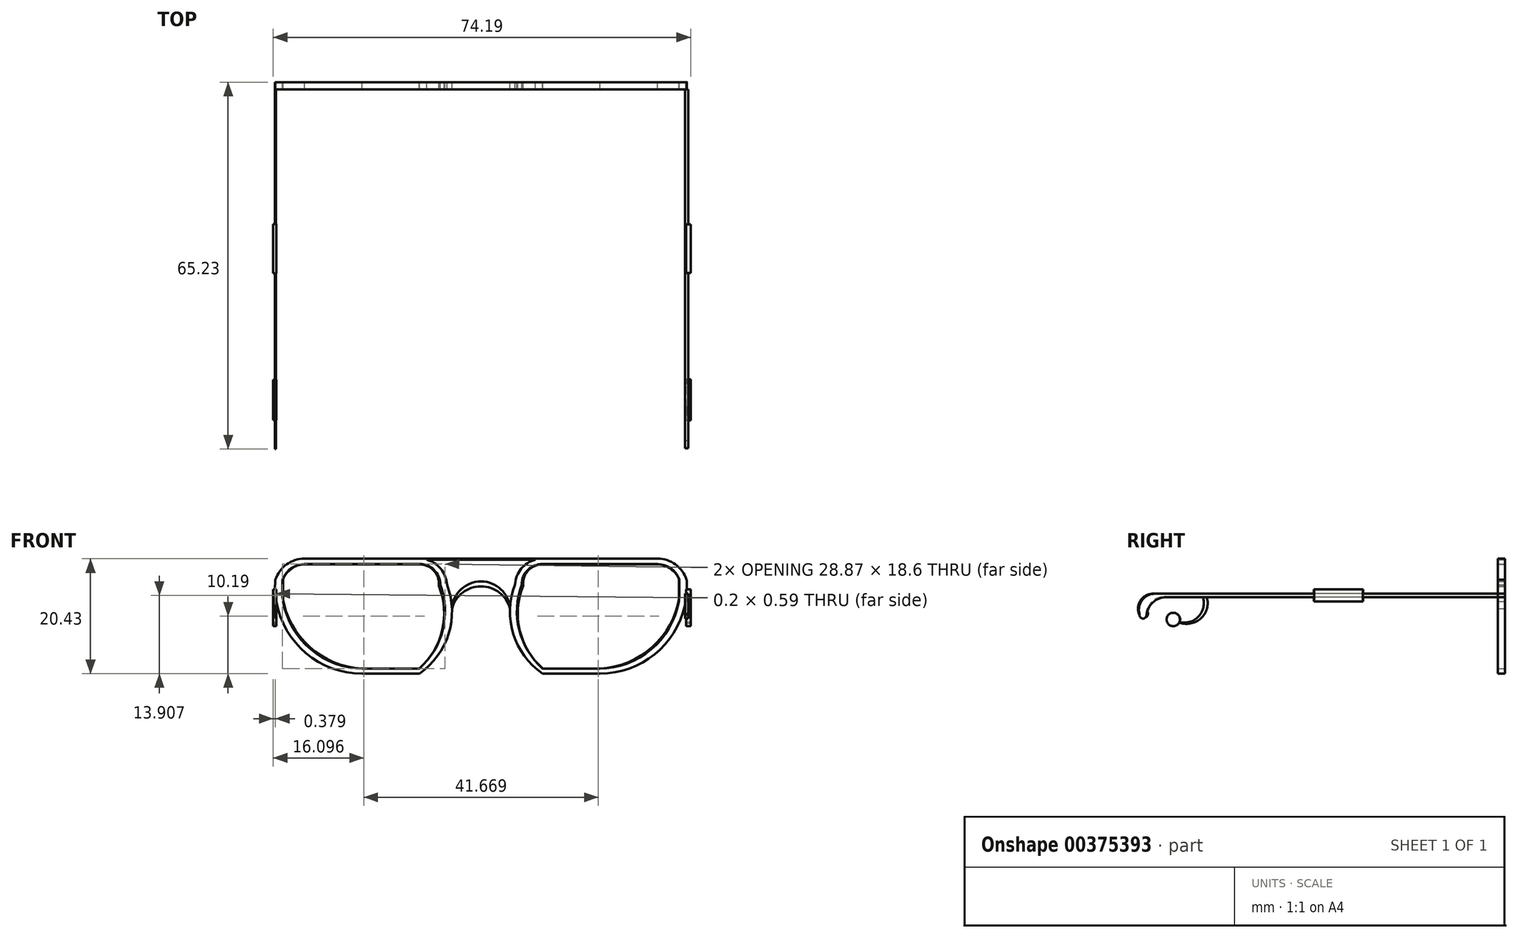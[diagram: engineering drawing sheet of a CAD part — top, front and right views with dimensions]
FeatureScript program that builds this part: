
annotation { "Feature Type Name" : "Feature", "Feature Type Description" : "" }
export const myFeature = defineFeature(function(context is Context, id is Id, definition is map)
    precondition{}
    {
        {
            var Q0;
            Q0=qCreatedBy(makeId("Front.planeOp"),FACE);
            var sketch = newSketch(context, id + "F0", { "sketchPlane" : qUnion([Q0])});
            skLineSegment(sketch, "E0", {"start": v(-10.94, 16.4) * mm, "end": v(-31.37, 16.4) * mm});
            skArc(sketch, "E1", {"start": v(-6.04, 11.8) * mm, "mid": v(-7.58, 15.07) * mm, "end": v(-10.94, 16.4) * mm});
            skArc(sketch, "E2", {"start": v(-10.94, -4.03) * mm, "mid": v(-5.75, 3.04) * mm, "end": v(-6.04, 11.8) * mm});
            skLineSegment(sketch, "E3", {"start": v(-10.94, -4.03) * mm, "end": v(-21.15, -4.03) * mm});
            skPoint(sketch, "E3.endSnap0", {"position": v(-21.15, 16.4) * mm});
            skArc(sketch, "E4", {"start": v(-31.37, 16.4) * mm, "mid": v(-34.57, 15.37) * mm, "end": v(-36.55, 12.66) * mm});
            skArc(sketch, "E5", {"start": v(-36.55, 12.66) * mm, "mid": v(-32.5, 0.94) * mm, "end": v(-21.15, -4.03) * mm});
            skLineSegment(sketch, "E6", {"start": v(0, 26.48) * mm, "end": v(0, -21.87) * mm, "construction": true});
            skArc(sketch, "E7.MirrorCS", {"start": v(6.04, 11.8) * mm, "mid": v(7.58, 15.07) * mm, "end": v(10.94, 16.4) * mm});
            skLineSegment(sketch, "E8.MirrorCS", {"start": v(10.94, 16.4) * mm, "end": v(31.37, 16.4) * mm});
            skArc(sketch, "E9.MirrorCS", {"start": v(31.37, 16.4) * mm, "mid": v(34.57, 15.37) * mm, "end": v(36.55, 12.66) * mm});
            skArc(sketch, "E10.MirrorCS", {"start": v(36.55, 12.66) * mm, "mid": v(32.5, 0.94) * mm, "end": v(21.15, -4.03) * mm});
            skLineSegment(sketch, "E11.MirrorCS", {"start": v(10.94, -4.03) * mm, "end": v(21.15, -4.03) * mm});
            skArc(sketch, "E12.MirrorCS", {"start": v(10.94, -4.03) * mm, "mid": v(5.75, 3.04) * mm, "end": v(6.04, 11.8) * mm});
            skLineSegment(sketch, "E13", {"start": v(-10.94, 16.4) * mm, "end": v(10.94, 16.4) * mm});
            skLineSegment(sketch, "E14", {"start": v(-9.67, 16.24) * mm, "end": v(9.67, 16.24) * mm});
            skPoint(sketch, "E15", {"position": v(-5.16, 7.53) * mm});
            skPoint(sketch, "E16", {"position": v(5.16, 7.53) * mm});
            skArc(sketch, "E17", {"start": v(5.16, 7.53) * mm, "mid": v(0, 12.36) * mm, "end": v(-5.16, 7.53) * mm});
            skArc(sketch, "E18", {"start": v(5.16, 7.53) * mm, "mid": v(0, 11.49) * mm, "end": v(-5.16, 7.53) * mm});
            skLineSegment(sketch, "E19.bottom", {"start": v(36.55, 12.66) * mm, "end": v(35.27, 12.66) * mm});
            skLineSegment(sketch, "E19.top", {"start": v(36.55, 9.58) * mm, "end": v(35.27, 9.58) * mm});
            skLineSegment(sketch, "E19.left", {"start": v(36.55, 12.66) * mm, "end": v(36.55, 9.58) * mm});
            skLineSegment(sketch, "E19.right", {"start": v(35.27, 12.66) * mm, "end": v(35.27, 9.58) * mm});
            skLineSegment(sketch, "E20.MirrorCS", {"start": v(-36.55, 12.66) * mm, "end": v(-35.27, 12.66) * mm});
            skLineSegment(sketch, "E21.MirrorCS", {"start": v(-36.55, 9.58) * mm, "end": v(-35.27, 9.58) * mm});
            skLineSegment(sketch, "E22.MirrorCS", {"start": v(-35.27, 12.66) * mm, "end": v(-35.27, 9.58) * mm});
            skLineSegment(sketch, "E23", {"start": v(-36.55, 12.66) * mm, "end": v(-36.55, 9.58) * mm});
            skArc(sketch, "E24", {"start": v(-31.37, 15.46) * mm, "mid": v(-33.7, 14.6) * mm, "end": v(-35.27, 12.66) * mm});
            skLineSegment(sketch, "E25", {"start": v(-31.37, 15.46) * mm, "end": v(-10.94, 15.46) * mm});
            skArc(sketch, "E26", {"start": v(-7.23, 11.8) * mm, "mid": v(-8.33, 14.4) * mm, "end": v(-10.94, 15.46) * mm});
            skArc(sketch, "E27", {"start": v(-35.27, 9.58) * mm, "mid": v(-30.46, 0.72) * mm, "end": v(-21.15, -3.14) * mm});
            skLineSegment(sketch, "E28", {"start": v(-21.15, -3.14) * mm, "end": v(-10.94, -3.14) * mm});
            skArc(sketch, "E29", {"start": v(-10.94, -3.14) * mm, "mid": v(-6.78, 3.76) * mm, "end": v(-7.23, 11.8) * mm});
            skLineSegment(sketch, "E30.MirrorCS", {"start": v(31.37, 15.46) * mm, "end": v(10.94, 15.46) * mm});
            skArc(sketch, "E31.MirrorCS", {"start": v(7.23, 11.8) * mm, "mid": v(8.33, 14.4) * mm, "end": v(10.94, 15.46) * mm});
            skArc(sketch, "E32.MirrorCS", {"start": v(10.94, -3.14) * mm, "mid": v(6.78, 3.76) * mm, "end": v(7.23, 11.8) * mm});
            skLineSegment(sketch, "E33.MirrorCS", {"start": v(21.15, -3.14) * mm, "end": v(10.94, -3.14) * mm});
            skArc(sketch, "E34.MirrorCS", {"start": v(35.27, 9.58) * mm, "mid": v(30.46, 0.72) * mm, "end": v(21.15, -3.14) * mm});
            skArc(sketch, "E35.MirrorCS", {"start": v(31.37, 15.46) * mm, "mid": v(33.7, 14.6) * mm, "end": v(35.27, 12.66) * mm});
            skSolve(sketch);
        }
        {
            var Q0;
            {var subQ0=sQuery(id+"F0.wireOp",EDGE,"E23");var subQ1=sQuery(id+"F0.wireOp",EDGE,"E5");var subQ3=makeQuery(id+"F0.imprint","INTERSECT",VERTEX,{"derivedFrom":[subQ1,subQ0]});Q0=makeQuery(id+"F0.imprint","IMPRINT",FACE,{"disambiguationData":[TD([[makeQuery(id+"F0.imprint","IMPRINT",EDGE,{"disambiguationData":[TD([[subQ3,1.0]])],"derivedFrom":subQ1}),1.0]])]});}
            var Q1;
            {var subQ0=sQuery(id+"F0.wireOp",EDGE,"E23");var subQ1=sQuery(id+"F0.wireOp",EDGE,"E5");var subQ2=makeQuery(id+"F0.imprint","INTERSECT",VERTEX,{"derivedFrom":[subQ1,subQ0]});Q1=makeQuery(id+"F0.imprint","IMPRINT",FACE,{"disambiguationData":[TD([[makeQuery(id+"F0.imprint","IMPRINT",EDGE,{"disambiguationData":[TD([[subQ2,-1.0]])],"derivedFrom":subQ1}),-1.0]])]});}
            var Q2;
            {var subQ0=sQuery(id+"F0.wireOp",EDGE,"E19.left");var subQ1=sQuery(id+"F0.wireOp",EDGE,"E10.MirrorCS");var subQ3=makeQuery(id+"F0.imprint","INTERSECT",VERTEX,{"derivedFrom":[subQ1,subQ0]});Q2=makeQuery(id+"F0.imprint","IMPRINT",FACE,{"disambiguationData":[TD([[makeQuery(id+"F0.imprint","IMPRINT",EDGE,{"disambiguationData":[TD([[subQ3,1.0]])],"derivedFrom":subQ1}),-1.0]])]});}
            var Q3;
            {var subQ0=sQuery(id+"F0.wireOp",EDGE,"E19.left");var subQ1=sQuery(id+"F0.wireOp",EDGE,"E10.MirrorCS");var subQ2=makeQuery(id+"F0.imprint","INTERSECT",VERTEX,{"derivedFrom":[subQ1,subQ0]});Q3=makeQuery(id+"F0.imprint","IMPRINT",FACE,{"disambiguationData":[TD([[makeQuery(id+"F0.imprint","IMPRINT",EDGE,{"disambiguationData":[TD([[subQ2,-1.0]])],"derivedFrom":subQ1}),1.0]])]});}
            var Q4;
            Q4=makeQuery(id+"F0.imprint","IMPRINT",FACE,{"disambiguationData":[TD([[makeQuery(id+"F0.imprint","IMPRINT",EDGE,{"derivedFrom":sQuery(id+"F0.wireOp",EDGE,"E17")}),1.0]])]});
            var Q5;
            {var subQ0=sQuery(id+"F0.wireOp",EDGE,"E13");Q5=makeQuery(id+"F0.imprint","IMPRINT",FACE,{"disambiguationData":[TD([[makeQuery(id+"F0.imprint","IMPRINT",EDGE,{"derivedFrom":subQ0}),-1.0]])]});}
            var Q6;
            {var subQ9=sQuery(id+"F0.wireOp",EDGE,"E0");Q6=makeQuery(id+"F0.imprint","IMPRINT",FACE,{"disambiguationData":[TD([[makeQuery(id+"F0.imprint","IMPRINT",EDGE,{"derivedFrom":subQ9}),1.0]])]});}
            var Q7;
            {var subQ10=sQuery(id+"F0.wireOp",EDGE,"E8.MirrorCS");Q7=makeQuery(id+"F0.imprint","IMPRINT",FACE,{"disambiguationData":[TD([[makeQuery(id+"F0.imprint","IMPRINT",EDGE,{"derivedFrom":subQ10}),-1.0]])]});}
            var Q8;
            {var subQ1=sQuery(id+"F0.wireOp",EDGE,"E19.bottom");Q8=makeQuery(id+"F0.imprint","IMPRINT",FACE,{"disambiguationData":[TD([[makeQuery(id+"F0.imprint","IMPRINT",EDGE,{"derivedFrom":subQ1}),1.0]])]});}
            var Q9;
            {var subQ6=sQuery(id+"F0.wireOp",EDGE,"E20.MirrorCS");Q9=makeQuery(id+"F0.imprint","IMPRINT",FACE,{"disambiguationData":[TD([[makeQuery(id+"F0.imprint","IMPRINT",EDGE,{"derivedFrom":subQ6}),-1.0]])]});}
            extrude(context, id + "F1", {"entities" : qUnion([Q0, Q1, Q2, Q3, Q4, Q5, Q6, Q7, Q8, Q9]), "depth" : 1.27 * mm});
        }
        {
            var Q0;
            Q0=makeQuery(id+"F1.opExtrude","SWEPT_FACE",FACE,{"disambiguationData":[OSD([sQuery(id+"F0.wireOp",EDGE,"E19.left")])]});
            var sketch = newSketch(context, id + "F2", { "sketchPlane" : qUnion([Q0])});
            skLineSegment(sketch, "E36", {"start": v(-1.27, 10.17) * mm, "end": v(-62.23, 10.17) * mm});
            skPoint(sketch, "E36.endSnap0", {"position": v(-0.64, 10.17) * mm});
            skLineSegment(sketch, "E37", {"start": v(-1.27, 9.58) * mm, "end": v(-60.15, 9.58) * mm});
            skArc(sketch, "E38", {"start": v(-62.23, 10.17) * mm, "mid": v(-64.52, 9.02) * mm, "end": v(-64.95, 6.48) * mm});
            skArc(sketch, "E39", {"start": v(-60.15, 9.58) * mm, "mid": v(-62.62, 8.6) * mm, "end": v(-63.76, 6.2) * mm});
            skArc(sketch, "E40", {"start": v(-64.95, 6.48) * mm, "mid": v(-64.5, 5.77) * mm, "end": v(-63.76, 6.2) * mm});
            skSolve(sketch);
        }
        {
            var Q0;
            Q0 = qSketchRegion(id + "F2", true);
            var Q1;
            Q1=makeQuery(id+"F2.imprint","IMPRINT",FACE,{"disambiguationData":[TD([[makeQuery(id+"F2.imprint","IMPRINT",EDGE,{"derivedFrom":sQuery(id+"F2.wireOp",EDGE,"E36")}),1.0]])]});
            extrude(context, id + "F3", {"entities" : qUnion([Q0, Q1]), "operationType" : NewBodyOperationType.ADD, "endBound" : BoundingType.SYMMETRIC, "depth" : 0.6 * mm});
        }
        {
            var Q0;
            Q0=makeQuery(id+"F1.opExtrude","SWEPT_FACE",FACE,{"disambiguationData":[OSD([sQuery(id+"F0.wireOp",EDGE,"E23")])]});
            var sketch = newSketch(context, id + "F4", { "sketchPlane" : qUnion([Q0])});
            skLineSegment(sketch, "E41", {"start": v(1.27, 10.17) * mm, "end": v(62.55, 10.17) * mm});
            skLineSegment(sketch, "E42", {"start": v(1.27, 9.58) * mm, "end": v(60.77, 9.58) * mm});
            skArc(sketch, "E43", {"start": v(64.99, 6.37) * mm, "mid": v(64.8, 8.94) * mm, "end": v(62.55, 10.17) * mm});
            skArc(sketch, "E44", {"start": v(63.56, 7.03) * mm, "mid": v(62.66, 8.85) * mm, "end": v(60.77, 9.58) * mm});
            skArc(sketch, "E45", {"start": v(63.56, 7.03) * mm, "mid": v(63.91, 5.92) * mm, "end": v(64.99, 6.37) * mm});
            skLineSegment(sketch, "E46", {"start": v(1.27, 10.17) * mm, "end": v(1.27, 9.58) * mm});
            skSolve(sketch);
        }
        {
            var Q0;
            Q0=makeQuery(id+"F4.imprint","IMPRINT",FACE,{"disambiguationData":[TD([[makeQuery(id+"F4.imprint","IMPRINT",EDGE,{"derivedFrom":sQuery(id+"F4.wireOp",EDGE,"E41")}),-1.0]])]});
            extrude(context, id + "F5", {"entities" : qUnion([Q0]), "endBound" : BoundingType.SYMMETRIC, "depth" : 0.2 * mm});
        }
        {
            var Q0;
            Q0=qCreatedBy(makeId("Front.planeOp"),FACE);
            var sketch = newSketch(context, id + "F6", { "sketchPlane" : qUnion([Q0])});
            skLineSegment(sketch, "E47", {"start": v(31.53, 15.4) * mm, "end": v(10.92, 15.4) * mm});
            skLineSegment(sketch, "E48", {"start": v(35.17, 12.78) * mm, "end": v(35.17, 8.82) * mm});
            skLineSegment(sketch, "E49", {"start": v(20.97, -3.13) * mm, "end": v(11, -3.13) * mm});
            skLineSegment(sketch, "E50", {"start": v(0, 25.35) * mm, "end": v(0, -13.64) * mm, "construction": true});
            skArc(sketch, "E51", {"start": v(35.17, 12.78) * mm, "mid": v(33.77, 14.67) * mm, "end": v(31.53, 15.4) * mm});
            skArc(sketch, "E52", {"start": v(20.97, -3.13) * mm, "mid": v(30.25, 0.26) * mm, "end": v(35.17, 8.82) * mm});
            skArc(sketch, "E53", {"start": v(10.92, 15.4) * mm, "mid": v(8.35, 14.24) * mm, "end": v(7.49, 11.56) * mm});
            skArc(sketch, "E54", {"start": v(7.49, 11.56) * mm, "mid": v(6.9, 3.66) * mm, "end": v(11, -3.13) * mm});
            skArc(sketch, "E55.MirrorCS", {"start": v(-10.92, 15.4) * mm, "mid": v(-8.35, 14.24) * mm, "end": v(-7.49, 11.56) * mm});
            skLineSegment(sketch, "E56.MirrorCS", {"start": v(-31.53, 15.4) * mm, "end": v(-10.92, 15.4) * mm});
            skArc(sketch, "E57.MirrorCS", {"start": v(-35.17, 12.78) * mm, "mid": v(-33.77, 14.67) * mm, "end": v(-31.53, 15.4) * mm});
            skLineSegment(sketch, "E58.MirrorCS", {"start": v(-35.17, 12.78) * mm, "end": v(-35.17, 8.82) * mm});
            skArc(sketch, "E59.MirrorCS", {"start": v(-20.97, -3.13) * mm, "mid": v(-30.25, 0.26) * mm, "end": v(-35.17, 8.82) * mm});
            skLineSegment(sketch, "E60.MirrorCS", {"start": v(-20.97, -3.13) * mm, "end": v(-11, -3.13) * mm});
            skArc(sketch, "E61.MirrorCS", {"start": v(-7.49, 11.56) * mm, "mid": v(-6.9, 3.66) * mm, "end": v(-11, -3.13) * mm});
            skSolve(sketch);
        }
        {
            var Q0;
            Q0 = qSketchRegion(id + "F6", true);
            var Q1;
            Q1=makeQuery(id+"F1.opExtrude","CAP_FACE",FACE,{"disambiguationData":[OSD([sQuery(id+"F0.wireOp",EDGE,"E0"),sQuery(id+"F0.wireOp",EDGE,"E1"),sQuery(id+"F0.wireOp",EDGE,"E2"),sQuery(id+"F0.wireOp",EDGE,"E3"),sQuery(id+"F0.wireOp",EDGE,"E4"),sQuery(id+"F0.wireOp",EDGE,"E5"),sQuery(id+"F0.wireOp",EDGE,"E7.MirrorCS"),sQuery(id+"F0.wireOp",EDGE,"E8.MirrorCS"),sQuery(id+"F0.wireOp",EDGE,"E9.MirrorCS"),sQuery(id+"F0.wireOp",EDGE,"E10.MirrorCS"),sQuery(id+"F0.wireOp",EDGE,"E11.MirrorCS"),sQuery(id+"F0.wireOp",EDGE,"E12.MirrorCS"),sQuery(id+"F0.wireOp",EDGE,"E13"),sQuery(id+"F0.wireOp",EDGE,"E14"),sQuery(id+"F0.wireOp",EDGE,"E19.top"),sQuery(id+"F0.wireOp",EDGE,"E21.MirrorCS"),sQuery(id+"F0.wireOp",EDGE,"E22.MirrorCS"),sQuery(id+"F0.wireOp",EDGE,"E19.left"),sQuery(id+"F0.wireOp",EDGE,"E23"),sQuery(id+"F0.wireOp",EDGE,"E24"),sQuery(id+"F0.wireOp",EDGE,"E25"),sQuery(id+"F0.wireOp",EDGE,"E26"),sQuery(id+"F0.wireOp",EDGE,"E27"),sQuery(id+"F0.wireOp",EDGE,"E28"),sQuery(id+"F0.wireOp",EDGE,"E29"),sQuery(id+"F0.wireOp",EDGE,"E30.MirrorCS"),sQuery(id+"F0.wireOp",EDGE,"E31.MirrorCS"),sQuery(id+"F0.wireOp",EDGE,"E32.MirrorCS"),sQuery(id+"F0.wireOp",EDGE,"E33.MirrorCS"),sQuery(id+"F0.wireOp",EDGE,"E34.MirrorCS"),sQuery(id+"F0.wireOp",EDGE,"E19.right"),sQuery(id+"F0.wireOp",EDGE,"E35.MirrorCS")])],"isStart":false});
            extrude(context, id + "F7", {"entities" : qUnion([Q0]), "endBound" : BoundingType.UP_TO_SURFACE, "endBoundEntityFace" : qUnion([Q1]), "depth" : 1.52 * mm});
        }
        {
            var Q0;
            Q0=makeQuery(id+"F5.opExtrude","CAP_FACE",FACE,{"disambiguationData":[OSD([sQuery(id+"F4.wireOp",EDGE,"E41"),sQuery(id+"F4.wireOp",EDGE,"E42"),sQuery(id+"F4.wireOp",EDGE,"E43"),sQuery(id+"F4.wireOp",EDGE,"E44"),sQuery(id+"F4.wireOp",EDGE,"E45"),sQuery(id+"F4.wireOp",EDGE,"E46")])],"isStart":false});
            var sketch = newSketch(context, id + "F8", { "sketchPlane" : qUnion([Q0])});
            skLineSegment(sketch, "E62.bottom", {"start": v(25.25, 10.94) * mm, "end": v(33.95, 10.94) * mm});
            skLineSegment(sketch, "E62.top", {"start": v(25.25, 8.86) * mm, "end": v(33.95, 8.86) * mm});
            skLineSegment(sketch, "E62.left", {"start": v(25.25, 10.94) * mm, "end": v(25.25, 8.86) * mm});
            skLineSegment(sketch, "E62.right", {"start": v(33.95, 10.94) * mm, "end": v(33.95, 8.86) * mm});
            skArc(sketch, "E63", {"start": v(53.02, 9.58) * mm, "mid": v(54.53, 5.46) * mm, "end": v(58.92, 5.6) * mm});
            skArc(sketch, "E64", {"start": v(53.63, 9.58) * mm, "mid": v(54.88, 5.73) * mm, "end": v(58.92, 5.6) * mm});
            skLineSegment(sketch, "E65", {"start": v(53.63, 9.58) * mm, "end": v(53.02, 9.58) * mm});
            skCircle(sketch, "E66", {"center": v(58.92, 5.6) * mm, "radius": 1.17 * mm});
            skSolve(sketch);
        }
        {
            var Q0;
            Q0 = qSketchRegion(id + "F8", true);
            extrude(context, id + "F9", {"entities" : qUnion([Q0]), "operationType" : NewBodyOperationType.ADD, "endBound" : BoundingType.SYMMETRIC, "depth" : 0.56 * mm});
        }
        {
            var Q0;
            Q0=makeQuery(id+"F3.opExtrude","CAP_FACE",FACE,{"disambiguationData":[OSD([sQuery(id+"F0.wireOp",EDGE,"E19.left"),sQuery(id+"F2.wireOp",EDGE,"E36"),sQuery(id+"F2.wireOp",EDGE,"E37"),sQuery(id+"F2.wireOp",EDGE,"E38"),sQuery(id+"F2.wireOp",EDGE,"E39"),sQuery(id+"F2.wireOp",EDGE,"E40")])],"isStart":false});
            var sketch = newSketch(context, id + "F10", { "sketchPlane" : qUnion([Q0])});
            skLineSegment(sketch, "E67.bottom", {"start": v(-25.3, 10.94) * mm, "end": v(-33.93, 10.94) * mm});
            skLineSegment(sketch, "E67.top", {"start": v(-25.3, 8.82) * mm, "end": v(-33.93, 8.82) * mm});
            skLineSegment(sketch, "E67.left", {"start": v(-25.3, 10.94) * mm, "end": v(-25.3, 8.82) * mm});
            skLineSegment(sketch, "E67.right", {"start": v(-33.93, 10.94) * mm, "end": v(-33.93, 8.82) * mm});
            skArc(sketch, "E68", {"start": v(-57.85, 5.08) * mm, "mid": v(-54.03, 5.82) * mm, "end": v(-53.01, 9.58) * mm});
            skArc(sketch, "E69", {"start": v(-57.85, 5.08) * mm, "mid": v(-54.48, 6.14) * mm, "end": v(-53.68, 9.58) * mm});
            skLineSegment(sketch, "E70", {"start": v(-53.68, 9.58) * mm, "end": v(-53.01, 9.58) * mm});
            skCircle(sketch, "E71", {"center": v(-58.97, 5.6) * mm, "radius": 1.2 * mm});
            skSolve(sketch);
        }
        {
            var Q0;
            Q0 = qSketchRegion(id + "F10", true);
            extrude(context, id + "F11", {"entities" : qUnion([Q0]), "operationType" : NewBodyOperationType.ADD, "endBound" : BoundingType.SYMMETRIC, "depth" : 0.81 * mm});
        }
    });
